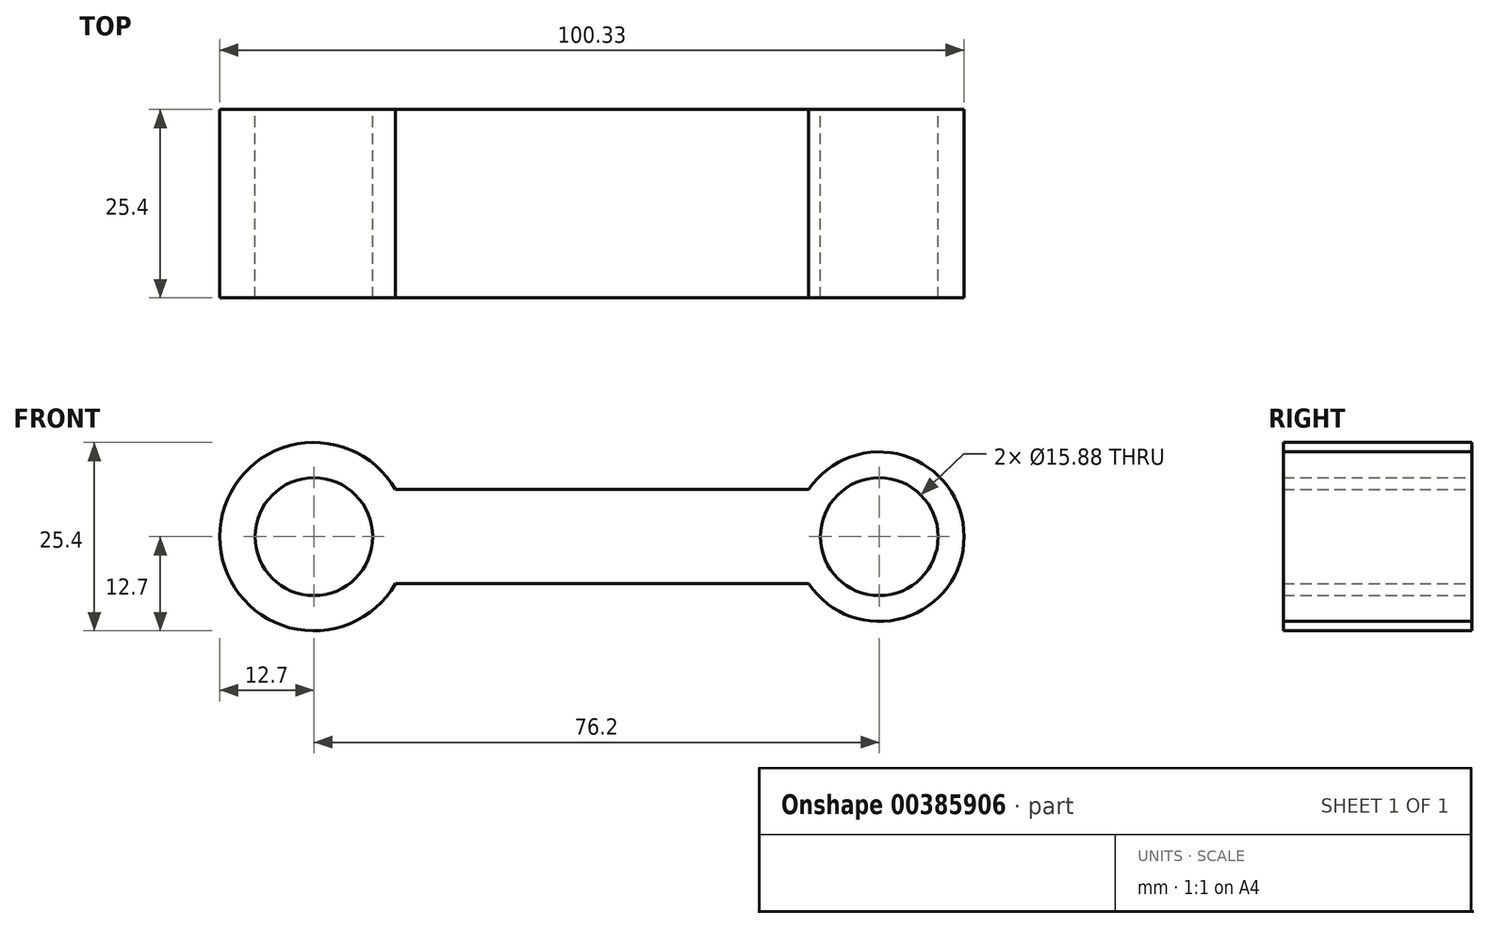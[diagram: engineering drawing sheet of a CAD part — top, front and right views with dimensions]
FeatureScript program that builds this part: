
annotation { "Feature Type Name" : "Feature", "Feature Type Description" : "" }
export const myFeature = defineFeature(function(context is Context, id is Id, definition is map)
    precondition{}
    {
        {
            var Q0;
            Q0=qCreatedBy(makeId("Front.planeOp"),FACE);
            var sketch = newSketch(context, id + "F0", { "sketchPlane" : qUnion([Q0])});
            skCircle(sketch, "E0", {"center": v(0, 0) * mm, "radius": 12.7 * mm});
            skCircle(sketch, "E1", {"center": v(76.2, 0) * mm, "radius": 11.43 * mm});
            skLineSegment(sketch, "E2", {"start": v(0, 0) * mm, "end": v(76.2, 0) * mm, "construction": true});
            skLineSegment(sketch, "E3", {"start": v(11, 6.35) * mm, "end": v(66.7, 6.35) * mm});
            skLineSegment(sketch, "E4.MirrorCS", {"start": v(11, -6.35) * mm, "end": v(66.7, -6.35) * mm});
            skCircle(sketch, "E5", {"center": v(0, 0) * mm, "radius": 7.94 * mm});
            skCircle(sketch, "E6", {"center": v(76.2, 0) * mm, "radius": 7.94 * mm});
            skSolve(sketch);
        }
        {
            var Q0;
            Q0 = qSketchRegion(id + "F0", true);
            extrude(context, id + "F1", {"entities" : qUnion([Q0]), "depth" : 25.4 * mm});
        }
    });
